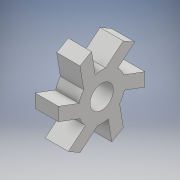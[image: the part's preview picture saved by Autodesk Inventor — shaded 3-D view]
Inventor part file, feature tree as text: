
AUTODESK INVENTOR PART (.ipt)
format: ipt  version: 2018 (Build 220112000, 112)  size: 131,072 bytes
history: native  units: mm
features: extrude x2, sketch x2, pattern_circular x1
ambient origin geometry x8: Origin, YZ Plane, XZ Plane, XY Plane, X Axis, Y Axis, Z Axis, Center Point
bodies: Solid1 (feature_tree)
feature tree (5):
  extrude  "Extrusion1"  Depth=3.5mm
  extrude  "Extrusion2"  Depth=3.5mm
  pattern_circular  "Circular Pattern1"  [2 undecoded]
  sketch  "Sketch1"  dims[d0=3.5mm d1=7.0mm]
  sketch  "Sketch2"  dims[d2=3.5mm d3=0.0mm d4=1.0mm d5=1.5mm d6=3.0mm d7=3.0mm d8=2.0mm d9=3.5mm d10=0.0mm d11=60.0mm d12=360.0deg]
note: 2 required parameter values undecoded (feature->parameter linkage not recoverable at this tier; creation-order binding heuristic only, values carry confidence <= 0.55)
